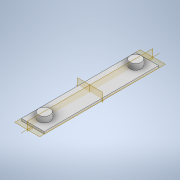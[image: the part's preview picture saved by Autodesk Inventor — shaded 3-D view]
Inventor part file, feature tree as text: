
AUTODESK INVENTOR PART (.ipt)
format: ipt  version: 2022.4 (Build 264492010, 492A)  size: 114,176 bytes
history: native  units: mm
features: extrude x2, sketch x2
ambient origin geometry x8: Origin, YZ Plane, XZ Plane, XY Plane, X Axis, Y Axis, Z Axis, Center Point
bodies: Solid1 (feature_tree)
feature tree (4):
  extrude  "Extrusion1"  Depth=50.0mm
  extrude  "Extrusion2"  Depth=2.5mm
  sketch  "Sketch1"  dims[d0=10.0mm d1=50.0mm]
  sketch  "Sketch2"  dims[d2=1.0mm d3=0.0mm d4=5.0mm d5=5.0mm d6=5.0mm d7=20.0mm d9=360.0deg d11=2.5mm d12=0.0mm]
